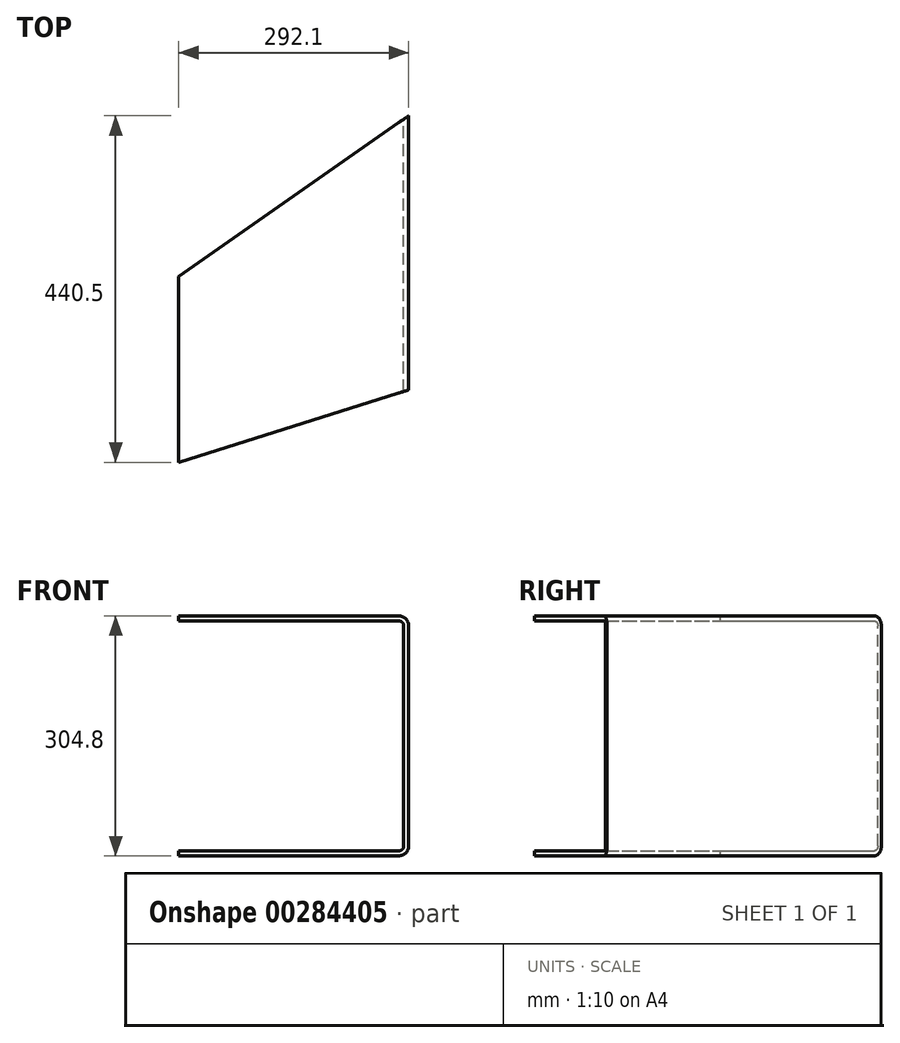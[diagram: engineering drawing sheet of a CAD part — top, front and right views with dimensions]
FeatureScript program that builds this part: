
annotation { "Feature Type Name" : "Feature", "Feature Type Description" : "" }
export const myFeature = defineFeature(function(context is Context, id is Id, definition is map)
    precondition{}
    {
        {
            var Q0;
            Q0=qCreatedBy(makeId("Front.planeOp"),FACE);
            var sketch = newSketch(context, id + "F0", { "sketchPlane" : qUnion([Q0])});
            skLineSegment(sketch, "E0.bottom", {"start": v(139.7, 146.05) * mm, "end": v(-139.7, 146.05) * mm});
            skLineSegment(sketch, "E0.top", {"start": v(139.7, -146.05) * mm, "end": v(-139.7, -146.05) * mm});
            skLineSegment(sketch, "E0.left", {"start": v(146.05, 139.7) * mm, "end": v(146.05, -139.7) * mm});
            skLineSegment(sketch, "E0.right", {"start": v(-146.05, 139.7) * mm, "end": v(-146.05, -139.7) * mm});
            skPoint(sketch, "E0.middle", {"position": v(0, 0) * mm});
            skPoint(sketch, "E1.visualSharp", {"position": v(-146.05, 146.05) * mm});
            skArc(sketch, "E1.filletArc", {"start": v(-139.7, 146.05) * mm, "mid": v(-144.2, 144.2) * mm, "end": v(-146.05, 139.7) * mm});
            skPoint(sketch, "E2.visualSharp", {"position": v(146.05, 146.05) * mm});
            skArc(sketch, "E2.filletArc", {"start": v(146.05, 139.7) * mm, "mid": v(144.2, 144.2) * mm, "end": v(139.7, 146.05) * mm});
            skPoint(sketch, "E3.visualSharp", {"position": v(146.05, -146.05) * mm});
            skArc(sketch, "E3.filletArc", {"start": v(139.7, -146.05) * mm, "mid": v(144.2, -144.2) * mm, "end": v(146.05, -139.7) * mm});
            skPoint(sketch, "E4.visualSharp", {"position": v(-146.05, -146.05) * mm});
            skArc(sketch, "E4.filletArc", {"start": v(-146.05, -139.7) * mm, "mid": v(-144.2, -144.2) * mm, "end": v(-139.7, -146.05) * mm});
            skArc(sketch, "E5.0", {"start": v(139.7, -152.4) * mm, "mid": v(148.68, -148.68) * mm, "end": v(152.4, -139.7) * mm});
            skLineSegment(sketch, "E5.1", {"start": v(152.4, 139.7) * mm, "end": v(152.4, -139.7) * mm});
            skLineSegment(sketch, "E5.2", {"start": v(139.7, -152.4) * mm, "end": v(-139.7, -152.4) * mm});
            skArc(sketch, "E5.3", {"start": v(152.4, 139.7) * mm, "mid": v(148.68, 148.68) * mm, "end": v(139.7, 152.4) * mm});
            skArc(sketch, "E5.4", {"start": v(-152.4, -139.7) * mm, "mid": v(-148.68, -148.68) * mm, "end": v(-139.7, -152.4) * mm});
            skLineSegment(sketch, "E5.5", {"start": v(-152.4, 139.7) * mm, "end": v(-152.4, -139.7) * mm});
            skArc(sketch, "E5.6", {"start": v(-139.7, 152.4) * mm, "mid": v(-148.68, 148.68) * mm, "end": v(-152.4, 139.7) * mm});
            skLineSegment(sketch, "E5.7", {"start": v(139.7, 152.4) * mm, "end": v(-139.7, 152.4) * mm});
            skSolve(sketch);
        }
        {
            var Q0;
            Q0=makeQuery(id+"F0.imprint","IMPRINT",FACE,{"disambiguationData":[TD([[makeQuery(id+"F0.imprint","IMPRINT",EDGE,{"derivedFrom":sQuery(id+"F0.wireOp",EDGE,"E0.bottom")}),-1.0]])]});
            extrude(context, id + "F1", {"entities" : qUnion([Q0]), "depth" : 444.5 * mm});
        }
        {
            var Q0;
            Q0=makeQuery(id+"F1.opExtrude","SWEPT_FACE",FACE,{"disambiguationData":[OSD([sQuery(id+"F0.wireOp",EDGE,"E5.7")])]});
            var sketch = newSketch(context, id + "F2", { "sketchPlane" : qUnion([Q0])});
            skLineSegment(sketch, "E6.0", {"start": v(152.4, -444.5) * mm, "end": v(152.4, 0) * mm});
            skLineSegment(sketch, "E7.0", {"start": v(152.4, -444.5) * mm, "end": v(139.7, -444.5) * mm});
            skLineSegment(sketch, "E8.0", {"start": v(139.7, -444.5) * mm, "end": v(-139.7, -444.5) * mm});
            skLineSegment(sketch, "E9.0", {"start": v(-139.7, -444.5) * mm, "end": v(-152.4, -444.5) * mm});
            skLineSegment(sketch, "E10", {"start": v(-152.4, -444.5) * mm, "end": v(152.4, -348.4) * mm});
            skLineSegment(sketch, "E11.0", {"start": v(-152.4, -444.5) * mm, "end": v(-152.4, 0) * mm});
            skLineSegment(sketch, "E12.0", {"start": v(139.7, 0) * mm, "end": v(-139.7, 0) * mm});
            skLineSegment(sketch, "E12.1", {"start": v(152.4, 0) * mm, "end": v(139.7, 0) * mm});
            skLineSegment(sketch, "E12.2", {"start": v(-139.7, 0) * mm, "end": v(-152.4, 0) * mm});
            skLineSegment(sketch, "E13", {"start": v(152.4, 0) * mm, "end": v(-152.4, -213.42) * mm});
            skSolve(sketch);
        }
        {
            var Q0;
            {var subQ0=sQuery(id+"F2.wireOp",EDGE,"E8.0");Q0=makeQuery(id+"F2.imprint","IMPRINT",FACE,{"disambiguationData":[TD([[makeQuery(id+"F2.imprint","IMPRINT",EDGE,{"derivedFrom":subQ0}),-1.0]])]});}
            var Q1;
            {var subQ0=sQuery(id+"F2.wireOp",EDGE,"E7.0");Q1=makeQuery(id+"F2.imprint","IMPRINT",FACE,{"disambiguationData":[TD([[makeQuery(id+"F2.imprint","IMPRINT",EDGE,{"derivedFrom":subQ0}),-1.0]])]});}
            var Q2;
            {var subQ0=sQuery(id+"F2.wireOp",EDGE,"E9.0");Q2=makeQuery(id+"F2.imprint","IMPRINT",FACE,{"disambiguationData":[TD([[makeQuery(id+"F2.imprint","IMPRINT",EDGE,{"derivedFrom":subQ0}),-1.0]])]});}
            var Q3;
            {var subQ0=sQuery(id+"F2.wireOp",EDGE,"E12.0");Q3=makeQuery(id+"F2.imprint","IMPRINT",FACE,{"disambiguationData":[TD([[makeQuery(id+"F2.imprint","IMPRINT",EDGE,{"derivedFrom":subQ0}),1.0]])]});}
            var Q4;
            {var subQ0=sQuery(id+"F2.wireOp",EDGE,"E12.2");Q4=makeQuery(id+"F2.imprint","IMPRINT",FACE,{"disambiguationData":[TD([[makeQuery(id+"F2.imprint","IMPRINT",EDGE,{"derivedFrom":subQ0}),1.0]])]});}
            var Q5;
            {var subQ0=sQuery(id+"F2.wireOp",EDGE,"E12.1");Q5=makeQuery(id+"F2.imprint","IMPRINT",FACE,{"disambiguationData":[TD([[makeQuery(id+"F2.imprint","IMPRINT",EDGE,{"derivedFrom":subQ0}),1.0]])]});}
            var Q6;
            {var subQ0=sQuery(id+"F2.wireOp",EDGE,"E11.0");var subQ5=sQuery(id+"F2.wireOp",EDGE,"E13");var subQ6=makeQuery(id+"F2.imprint","INTERSECT",VERTEX,{"derivedFrom":[subQ0,subQ5]});Q6=makeQuery(id+"F2.imprint","IMPRINT",FACE,{"disambiguationData":[TD([[makeQuery(id+"F2.imprint","IMPRINT",EDGE,{"disambiguationData":[TD([[subQ6,1.0]])],"derivedFrom":subQ0}),-1.0]])]});}
            extrude(context, id + "F3", {"entities" : qUnion([Q0, Q1, Q2, Q3, Q4, Q5, Q6]), "operationType" : NewBodyOperationType.REMOVE, "endBound" : BoundingType.THROUGH_ALL, "oppositeDirection" : true, "depth" : 25.4 * mm});
        }
    });
